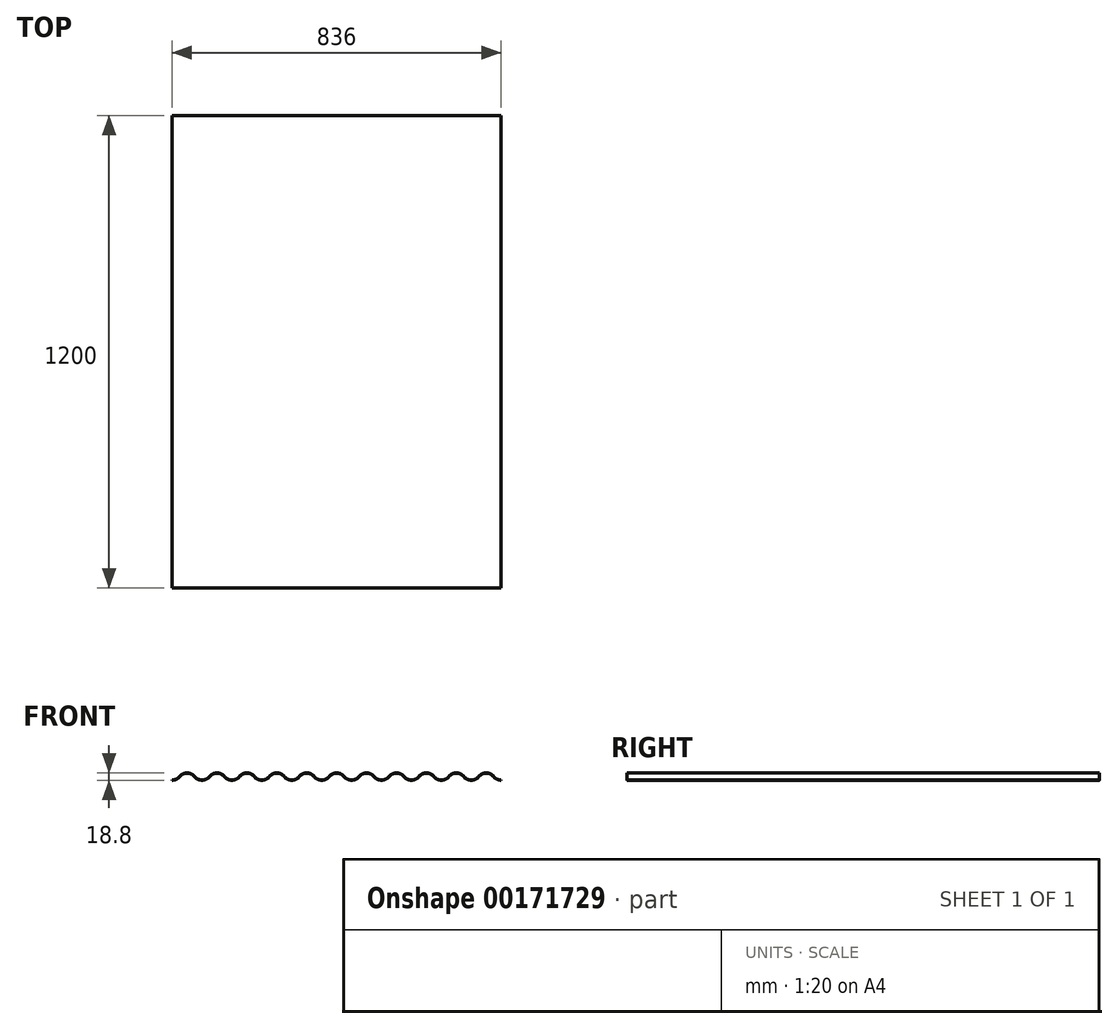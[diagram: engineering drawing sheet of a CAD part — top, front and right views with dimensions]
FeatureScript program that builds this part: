
annotation { "Feature Type Name" : "Feature", "Feature Type Description" : "" }
export const myFeature = defineFeature(function(context is Context, id is Id, definition is map)
    precondition{}
    {
        {
            var Q0;
            Q0=qCreatedBy(makeId("Front.planeOp"),FACE);
            var sketch = newSketch(context, id + "F0", { "sketchPlane" : qUnion([Q0])});
            skLineSegment(sketch, "E0", {"start": v(-38, 0) * mm, "end": v(38, 0) * mm, "construction": true});
            skArc(sketch, "E1", {"start": v(19, 9) * mm, "mid": v(27.49, 2.36) * mm, "end": v(38, 0) * mm});
            skArc(sketch, "E2", {"start": v(-38, 0) * mm, "mid": v(-27.49, 2.36) * mm, "end": v(-19, 9) * mm});
            skArc(sketch, "E3", {"start": v(19, 9) * mm, "mid": v(0, 18) * mm, "end": v(-19, 9) * mm});
            skLineSegment(sketch, "E4", {"start": v(-38, 0) * mm, "end": v(-38, 18) * mm, "construction": true});
            skLineSegment(sketch, "E5", {"start": v(-38, 18) * mm, "end": v(38, 18) * mm, "construction": true});
            skLineSegment(sketch, "E6", {"start": v(38, 18) * mm, "end": v(38, 0) * mm, "construction": true});
            skLineSegment(sketch, "E7", {"start": v(0, 0) * mm, "end": v(0, 18) * mm, "construction": true});
            skLineSegment(sketch, "E8", {"start": v(-19, 9) * mm, "end": v(19, 9) * mm, "construction": true});
            skArc(sketch, "E9.0", {"start": v(18.38, 8.5) * mm, "mid": v(27.15, 1.64) * mm, "end": v(38, -0.8) * mm});
            skArc(sketch, "E9.1", {"start": v(18.38, 8.5) * mm, "mid": v(0, 17.2) * mm, "end": v(-18.38, 8.5) * mm});
            skArc(sketch, "E9.2", {"start": v(-38, -0.8) * mm, "mid": v(-27.15, 1.64) * mm, "end": v(-18.38, 8.5) * mm});
            skArc(sketch, "E10.1.0.0", {"start": v(94.38, 8.5) * mm, "mid": v(76, 17.2) * mm, "end": v(57.62, 8.5) * mm});
            skArc(sketch, "E10.1.0.1", {"start": v(95, 9) * mm, "mid": v(76, 18) * mm, "end": v(57, 9) * mm});
            skArc(sketch, "E10.1.0.2", {"start": v(38, 0) * mm, "mid": v(48.51, 2.36) * mm, "end": v(57, 9) * mm});
            skArc(sketch, "E10.1.0.3", {"start": v(38, -0.8) * mm, "mid": v(48.85, 1.64) * mm, "end": v(57.62, 8.5) * mm});
            skArc(sketch, "E10.1.0.4", {"start": v(94.38, 8.5) * mm, "mid": v(103.15, 1.64) * mm, "end": v(114, -0.8) * mm});
            skArc(sketch, "E10.1.0.5", {"start": v(95, 9) * mm, "mid": v(103.49, 2.36) * mm, "end": v(114, 0) * mm});
            skLineSegment(sketch, "E10.1.0.6", {"start": v(38, 0) * mm, "end": v(114, 0) * mm, "construction": true});
            skArc(sketch, "E10.2.0.0", {"start": v(170.38, 8.5) * mm, "mid": v(152, 17.2) * mm, "end": v(133.62, 8.5) * mm});
            skArc(sketch, "E10.2.0.1", {"start": v(171, 9) * mm, "mid": v(152, 18) * mm, "end": v(133, 9) * mm});
            skArc(sketch, "E10.2.0.2", {"start": v(114, 0) * mm, "mid": v(124.51, 2.36) * mm, "end": v(133, 9) * mm});
            skArc(sketch, "E10.2.0.3", {"start": v(114, -0.8) * mm, "mid": v(124.85, 1.64) * mm, "end": v(133.62, 8.5) * mm});
            skArc(sketch, "E10.2.0.4", {"start": v(170.38, 8.5) * mm, "mid": v(179.15, 1.64) * mm, "end": v(190, -0.8) * mm});
            skArc(sketch, "E10.2.0.5", {"start": v(171, 9) * mm, "mid": v(179.49, 2.36) * mm, "end": v(190, 0) * mm});
            skLineSegment(sketch, "E10.2.0.6", {"start": v(114, 0) * mm, "end": v(190, 0) * mm, "construction": true});
            skArc(sketch, "E10.3.0.0", {"start": v(246.38, 8.5) * mm, "mid": v(228, 17.2) * mm, "end": v(209.62, 8.5) * mm});
            skArc(sketch, "E10.3.0.1", {"start": v(247, 9) * mm, "mid": v(228, 18) * mm, "end": v(209, 9) * mm});
            skArc(sketch, "E10.3.0.2", {"start": v(190, 0) * mm, "mid": v(200.51, 2.36) * mm, "end": v(209, 9) * mm});
            skArc(sketch, "E10.3.0.3", {"start": v(190, -0.8) * mm, "mid": v(200.85, 1.64) * mm, "end": v(209.62, 8.5) * mm});
            skArc(sketch, "E10.3.0.4", {"start": v(246.38, 8.5) * mm, "mid": v(255.15, 1.64) * mm, "end": v(266, -0.8) * mm});
            skArc(sketch, "E10.3.0.5", {"start": v(247, 9) * mm, "mid": v(255.49, 2.36) * mm, "end": v(266, 0) * mm});
            skLineSegment(sketch, "E10.3.0.6", {"start": v(190, 0) * mm, "end": v(266, 0) * mm, "construction": true});
            skArc(sketch, "E10.4.0.0", {"start": v(322.38, 8.5) * mm, "mid": v(304, 17.2) * mm, "end": v(285.62, 8.5) * mm});
            skArc(sketch, "E10.4.0.1", {"start": v(323, 9) * mm, "mid": v(304, 18) * mm, "end": v(285, 9) * mm});
            skArc(sketch, "E10.4.0.2", {"start": v(266, 0) * mm, "mid": v(276.51, 2.36) * mm, "end": v(285, 9) * mm});
            skArc(sketch, "E10.4.0.3", {"start": v(266, -0.8) * mm, "mid": v(276.85, 1.64) * mm, "end": v(285.62, 8.5) * mm});
            skArc(sketch, "E10.4.0.4", {"start": v(322.38, 8.5) * mm, "mid": v(331.15, 1.64) * mm, "end": v(342, -0.8) * mm});
            skArc(sketch, "E10.4.0.5", {"start": v(323, 9) * mm, "mid": v(331.49, 2.36) * mm, "end": v(342, 0) * mm});
            skLineSegment(sketch, "E10.4.0.6", {"start": v(266, 0) * mm, "end": v(342, 0) * mm, "construction": true});
            skArc(sketch, "E10.5.0.0", {"start": v(398.38, 8.5) * mm, "mid": v(380, 17.2) * mm, "end": v(361.62, 8.5) * mm});
            skArc(sketch, "E10.5.0.1", {"start": v(399, 9) * mm, "mid": v(380, 18) * mm, "end": v(361, 9) * mm});
            skArc(sketch, "E10.5.0.2", {"start": v(342, 0) * mm, "mid": v(352.51, 2.36) * mm, "end": v(361, 9) * mm});
            skArc(sketch, "E10.5.0.3", {"start": v(342, -0.8) * mm, "mid": v(352.85, 1.64) * mm, "end": v(361.62, 8.5) * mm});
            skArc(sketch, "E10.5.0.4", {"start": v(398.38, 8.5) * mm, "mid": v(407.15, 1.64) * mm, "end": v(418, -0.8) * mm});
            skArc(sketch, "E10.5.0.5", {"start": v(399, 9) * mm, "mid": v(407.49, 2.36) * mm, "end": v(418, 0) * mm});
            skLineSegment(sketch, "E10.5.0.6", {"start": v(342, 0) * mm, "end": v(418, 0) * mm, "construction": true});
            skArc(sketch, "E10.6.0.0", {"start": v(474.38, 8.5) * mm, "mid": v(456, 17.2) * mm, "end": v(437.62, 8.5) * mm});
            skArc(sketch, "E10.6.0.1", {"start": v(475, 9) * mm, "mid": v(456, 18) * mm, "end": v(437, 9) * mm});
            skArc(sketch, "E10.6.0.2", {"start": v(418, 0) * mm, "mid": v(428.51, 2.36) * mm, "end": v(437, 9) * mm});
            skArc(sketch, "E10.6.0.3", {"start": v(418, -0.8) * mm, "mid": v(428.85, 1.64) * mm, "end": v(437.62, 8.5) * mm});
            skArc(sketch, "E10.6.0.4", {"start": v(474.38, 8.5) * mm, "mid": v(483.15, 1.64) * mm, "end": v(494, -0.8) * mm});
            skArc(sketch, "E10.6.0.5", {"start": v(475, 9) * mm, "mid": v(483.49, 2.36) * mm, "end": v(494, 0) * mm});
            skLineSegment(sketch, "E10.6.0.6", {"start": v(418, 0) * mm, "end": v(494, 0) * mm, "construction": true});
            skArc(sketch, "E10.7.0.0", {"start": v(550.38, 8.5) * mm, "mid": v(532, 17.2) * mm, "end": v(513.62, 8.5) * mm});
            skArc(sketch, "E10.7.0.1", {"start": v(551, 9) * mm, "mid": v(532, 18) * mm, "end": v(513, 9) * mm});
            skArc(sketch, "E10.7.0.2", {"start": v(494, 0) * mm, "mid": v(504.51, 2.36) * mm, "end": v(513, 9) * mm});
            skArc(sketch, "E10.7.0.3", {"start": v(494, -0.8) * mm, "mid": v(504.85, 1.64) * mm, "end": v(513.62, 8.5) * mm});
            skArc(sketch, "E10.7.0.4", {"start": v(550.38, 8.5) * mm, "mid": v(559.15, 1.64) * mm, "end": v(570, -0.8) * mm});
            skArc(sketch, "E10.7.0.5", {"start": v(551, 9) * mm, "mid": v(559.49, 2.36) * mm, "end": v(570, 0) * mm});
            skLineSegment(sketch, "E10.7.0.6", {"start": v(494, 0) * mm, "end": v(570, 0) * mm, "construction": true});
            skArc(sketch, "E10.8.0.0", {"start": v(626.38, 8.5) * mm, "mid": v(608, 17.2) * mm, "end": v(589.62, 8.5) * mm});
            skArc(sketch, "E10.8.0.1", {"start": v(627, 9) * mm, "mid": v(608, 18) * mm, "end": v(589, 9) * mm});
            skArc(sketch, "E10.8.0.2", {"start": v(570, 0) * mm, "mid": v(580.51, 2.36) * mm, "end": v(589, 9) * mm});
            skArc(sketch, "E10.8.0.3", {"start": v(570, -0.8) * mm, "mid": v(580.85, 1.64) * mm, "end": v(589.62, 8.5) * mm});
            skArc(sketch, "E10.8.0.4", {"start": v(626.38, 8.5) * mm, "mid": v(635.15, 1.64) * mm, "end": v(646, -0.8) * mm});
            skArc(sketch, "E10.8.0.5", {"start": v(627, 9) * mm, "mid": v(635.49, 2.36) * mm, "end": v(646, 0) * mm});
            skLineSegment(sketch, "E10.8.0.6", {"start": v(570, 0) * mm, "end": v(646, 0) * mm, "construction": true});
            skArc(sketch, "E10.9.0.0", {"start": v(702.38, 8.5) * mm, "mid": v(684, 17.2) * mm, "end": v(665.62, 8.5) * mm});
            skArc(sketch, "E10.9.0.1", {"start": v(703, 9) * mm, "mid": v(684, 18) * mm, "end": v(665, 9) * mm});
            skArc(sketch, "E10.9.0.2", {"start": v(646, 0) * mm, "mid": v(656.51, 2.36) * mm, "end": v(665, 9) * mm});
            skArc(sketch, "E10.9.0.3", {"start": v(646, -0.8) * mm, "mid": v(656.85, 1.64) * mm, "end": v(665.62, 8.5) * mm});
            skArc(sketch, "E10.9.0.4", {"start": v(702.38, 8.5) * mm, "mid": v(711.15, 1.64) * mm, "end": v(722, -0.8) * mm});
            skArc(sketch, "E10.9.0.5", {"start": v(703, 9) * mm, "mid": v(711.49, 2.36) * mm, "end": v(722, 0) * mm});
            skLineSegment(sketch, "E10.9.0.6", {"start": v(646, 0) * mm, "end": v(722, 0) * mm, "construction": true});
            skArc(sketch, "E10.10.0.0", {"start": v(778.38, 8.5) * mm, "mid": v(760, 17.2) * mm, "end": v(741.62, 8.5) * mm});
            skArc(sketch, "E10.10.0.1", {"start": v(779, 9) * mm, "mid": v(760, 18) * mm, "end": v(741, 9) * mm});
            skArc(sketch, "E10.10.0.2", {"start": v(722, 0) * mm, "mid": v(732.51, 2.36) * mm, "end": v(741, 9) * mm});
            skArc(sketch, "E10.10.0.3", {"start": v(722, -0.8) * mm, "mid": v(732.85, 1.64) * mm, "end": v(741.62, 8.5) * mm});
            skArc(sketch, "E10.10.0.4", {"start": v(778.38, 8.5) * mm, "mid": v(787.15, 1.64) * mm, "end": v(798, -0.8) * mm});
            skArc(sketch, "E10.10.0.5", {"start": v(779, 9) * mm, "mid": v(787.49, 2.36) * mm, "end": v(798, 0) * mm});
            skLineSegment(sketch, "E10.10.0.6", {"start": v(722, 0) * mm, "end": v(798, 0) * mm, "construction": true});
            skLineSegment(sketch, "E10.direction1", {"start": v(-38, -0.8) * mm, "end": v(38, -0.8) * mm, "construction": true});
            skLineSegment(sketch, "E11", {"start": v(798, 0) * mm, "end": v(798, -0.8) * mm});
            skLineSegment(sketch, "E12", {"start": v(-38, -0.8) * mm, "end": v(-38, 0) * mm});
            skSolve(sketch);
        }
        {
            var Q0;
            Q0=makeQuery(id+"F0.imprint","IMPRINT",FACE,{"disambiguationData":[TD([[makeQuery(id+"F0.imprint","IMPRINT",EDGE,{"derivedFrom":sQuery(id+"F0.wireOp",EDGE,"E1")}),-1.0]])]});
            extrude(context, id + "F1", {"entities" : qUnion([Q0]), "depth" : 1200 * mm});
        }
    });
